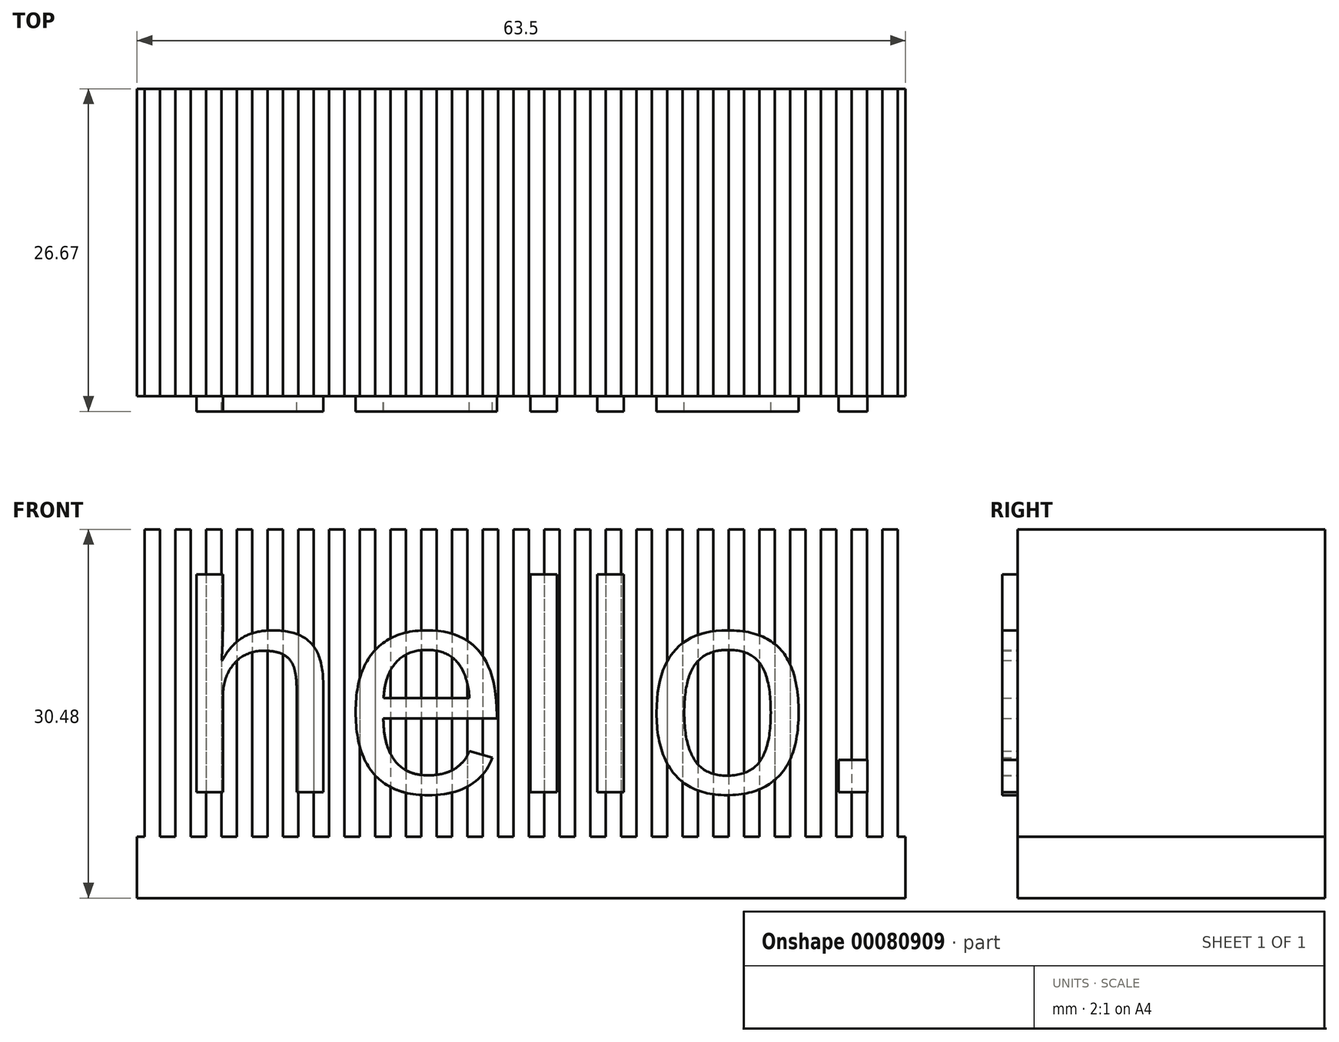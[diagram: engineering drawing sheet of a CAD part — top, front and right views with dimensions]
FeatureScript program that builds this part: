
annotation { "Feature Type Name" : "Feature", "Feature Type Description" : "" }
export const myFeature = defineFeature(function(context is Context, id is Id, definition is map)
    precondition{}
    {
        {
            var Q0;
            Q0=qCreatedBy(makeId("Top.planeOp"),FACE);
            var sketch = newSketch(context, id + "F0", { "sketchPlane" : qUnion([Q0])});
            skLineSegment(sketch, "E0.bottom", {"start": v(31.75, 12.7) * mm, "end": v(-31.75, 12.7) * mm});
            skLineSegment(sketch, "E0.top", {"start": v(31.75, -12.7) * mm, "end": v(-31.75, -12.7) * mm});
            skLineSegment(sketch, "E0.left", {"start": v(31.75, 12.7) * mm, "end": v(31.75, -12.7) * mm});
            skLineSegment(sketch, "E0.right", {"start": v(-31.75, 12.7) * mm, "end": v(-31.75, -12.7) * mm});
            skPoint(sketch, "E0.middle", {"position": v(0, 0) * mm});
            skSolve(sketch);
        }
        {
            var Q0;
            Q0=makeQuery(id+"F0.imprint","IMPRINT",FACE,{"disambiguationData":[TD([[makeQuery(id+"F0.imprint","IMPRINT",EDGE,{"derivedFrom":sQuery(id+"F0.wireOp",EDGE,"E0.bottom")}),1.0]])]});
            extrude(context, id + "F1", {"entities" : qUnion([Q0]), "depth" : 5.08 * mm});
        }
        {
            var Q0;
            Q0=makeQuery(id+"F1.opExtrude","CAP_FACE",FACE,{"disambiguationData":[OSD([sQuery(id+"F0.wireOp",EDGE,"E0.bottom"),sQuery(id+"F0.wireOp",EDGE,"E0.top"),sQuery(id+"F0.wireOp",EDGE,"E0.left"),sQuery(id+"F0.wireOp",EDGE,"E0.right")])],"isStart":false});
            var sketch = newSketch(context, id + "F2", { "sketchPlane" : qUnion([Q0])});
            skLineSegment(sketch, "E1.bottom", {"start": v(-29.84, -12.7) * mm, "end": v(-31.12, -12.7) * mm});
            skLineSegment(sketch, "E1.top", {"start": v(-29.84, 12.7) * mm, "end": v(-31.12, 12.7) * mm});
            skLineSegment(sketch, "E1.left", {"start": v(-29.84, -12.7) * mm, "end": v(-29.84, 12.7) * mm});
            skLineSegment(sketch, "E1.right", {"start": v(-31.12, -12.7) * mm, "end": v(-31.12, 12.7) * mm});
            skPoint(sketch, "E1.middle", {"position": v(-30.48, 0) * mm});
            skLineSegment(sketch, "E2.1.0.0", {"start": v(-28.57, -12.7) * mm, "end": v(-28.57, 12.7) * mm});
            skLineSegment(sketch, "E2.1.0.1", {"start": v(-27.3, -12.7) * mm, "end": v(-27.3, 12.7) * mm});
            skLineSegment(sketch, "E2.1.0.2", {"start": v(-27.3, 12.7) * mm, "end": v(-28.57, 12.7) * mm});
            skLineSegment(sketch, "E2.1.0.3", {"start": v(-27.3, -12.7) * mm, "end": v(-28.57, -12.7) * mm});
            skLineSegment(sketch, "E2.2.0.0", {"start": v(-26.04, -12.7) * mm, "end": v(-26.04, 12.7) * mm});
            skLineSegment(sketch, "E2.2.0.1", {"start": v(-24.77, -12.7) * mm, "end": v(-24.77, 12.7) * mm});
            skLineSegment(sketch, "E2.2.0.2", {"start": v(-24.77, 12.7) * mm, "end": v(-26.04, 12.7) * mm});
            skLineSegment(sketch, "E2.2.0.3", {"start": v(-24.77, -12.7) * mm, "end": v(-26.04, -12.7) * mm});
            skLineSegment(sketch, "E2.3.0.0", {"start": v(-23.5, -12.7) * mm, "end": v(-23.5, 12.7) * mm});
            skLineSegment(sketch, "E2.3.0.1", {"start": v(-22.22, -12.7) * mm, "end": v(-22.22, 12.7) * mm});
            skLineSegment(sketch, "E2.3.0.2", {"start": v(-22.22, 12.7) * mm, "end": v(-23.5, 12.7) * mm});
            skLineSegment(sketch, "E2.3.0.3", {"start": v(-22.22, -12.7) * mm, "end": v(-23.5, -12.7) * mm});
            skLineSegment(sketch, "E2.4.0.0", {"start": v(-20.95, -12.7) * mm, "end": v(-20.95, 12.7) * mm});
            skLineSegment(sketch, "E2.4.0.1", {"start": v(-19.68, -12.7) * mm, "end": v(-19.68, 12.7) * mm});
            skLineSegment(sketch, "E2.4.0.2", {"start": v(-19.68, 12.7) * mm, "end": v(-20.95, 12.7) * mm});
            skLineSegment(sketch, "E2.4.0.3", {"start": v(-19.68, -12.7) * mm, "end": v(-20.95, -12.7) * mm});
            skLineSegment(sketch, "E2.5.0.0", {"start": v(-18.41, -12.7) * mm, "end": v(-18.41, 12.7) * mm});
            skLineSegment(sketch, "E2.5.0.1", {"start": v(-17.14, -12.7) * mm, "end": v(-17.14, 12.7) * mm});
            skLineSegment(sketch, "E2.5.0.2", {"start": v(-17.14, 12.7) * mm, "end": v(-18.41, 12.7) * mm});
            skLineSegment(sketch, "E2.5.0.3", {"start": v(-17.14, -12.7) * mm, "end": v(-18.41, -12.7) * mm});
            skLineSegment(sketch, "E2.6.0.0", {"start": v(-15.87, -12.7) * mm, "end": v(-15.87, 12.7) * mm});
            skLineSegment(sketch, "E2.6.0.1", {"start": v(-14.6, -12.7) * mm, "end": v(-14.6, 12.7) * mm});
            skLineSegment(sketch, "E2.6.0.2", {"start": v(-14.6, 12.7) * mm, "end": v(-15.87, 12.7) * mm});
            skLineSegment(sketch, "E2.6.0.3", {"start": v(-14.6, -12.7) * mm, "end": v(-15.87, -12.7) * mm});
            skLineSegment(sketch, "E2.7.0.0", {"start": v(-13.33, -12.7) * mm, "end": v(-13.33, 12.7) * mm});
            skLineSegment(sketch, "E2.7.0.1", {"start": v(-12.06, -12.7) * mm, "end": v(-12.06, 12.7) * mm});
            skLineSegment(sketch, "E2.7.0.2", {"start": v(-12.06, 12.7) * mm, "end": v(-13.33, 12.7) * mm});
            skLineSegment(sketch, "E2.7.0.3", {"start": v(-12.06, -12.7) * mm, "end": v(-13.33, -12.7) * mm});
            skLineSegment(sketch, "E2.8.0.0", {"start": v(-10.8, -12.7) * mm, "end": v(-10.8, 12.7) * mm});
            skLineSegment(sketch, "E2.8.0.1", {"start": v(-9.52, -12.7) * mm, "end": v(-9.52, 12.7) * mm});
            skLineSegment(sketch, "E2.8.0.2", {"start": v(-9.52, 12.7) * mm, "end": v(-10.8, 12.7) * mm});
            skLineSegment(sketch, "E2.8.0.3", {"start": v(-9.52, -12.7) * mm, "end": v(-10.8, -12.7) * mm});
            skLineSegment(sketch, "E2.9.0.0", {"start": v(-8.25, -12.7) * mm, "end": v(-8.25, 12.7) * mm});
            skLineSegment(sketch, "E2.9.0.1", {"start": v(-6.98, -12.7) * mm, "end": v(-6.98, 12.7) * mm});
            skLineSegment(sketch, "E2.9.0.2", {"start": v(-6.98, 12.7) * mm, "end": v(-8.25, 12.7) * mm});
            skLineSegment(sketch, "E2.9.0.3", {"start": v(-6.98, -12.7) * mm, "end": v(-8.25, -12.7) * mm});
            skLineSegment(sketch, "E2.10.0.0", {"start": v(-5.71, -12.7) * mm, "end": v(-5.71, 12.7) * mm});
            skLineSegment(sketch, "E2.10.0.1", {"start": v(-4.44, -12.7) * mm, "end": v(-4.44, 12.7) * mm});
            skLineSegment(sketch, "E2.10.0.2", {"start": v(-4.44, 12.7) * mm, "end": v(-5.71, 12.7) * mm});
            skLineSegment(sketch, "E2.10.0.3", {"start": v(-4.44, -12.7) * mm, "end": v(-5.71, -12.7) * mm});
            skLineSegment(sketch, "E2.11.0.0", {"start": v(-3.17, -12.7) * mm, "end": v(-3.17, 12.7) * mm});
            skLineSegment(sketch, "E2.11.0.1", {"start": v(-1.9, -12.7) * mm, "end": v(-1.9, 12.7) * mm});
            skLineSegment(sketch, "E2.11.0.2", {"start": v(-1.9, 12.7) * mm, "end": v(-3.17, 12.7) * mm});
            skLineSegment(sketch, "E2.11.0.3", {"start": v(-1.9, -12.7) * mm, "end": v(-3.17, -12.7) * mm});
            skLineSegment(sketch, "E2.12.0.0", {"start": v(-0.63, -12.7) * mm, "end": v(-0.63, 12.7) * mm});
            skLineSegment(sketch, "E2.12.0.1", {"start": v(0.64, -12.7) * mm, "end": v(0.64, 12.7) * mm});
            skLineSegment(sketch, "E2.12.0.2", {"start": v(0.64, 12.7) * mm, "end": v(-0.63, 12.7) * mm});
            skLineSegment(sketch, "E2.12.0.3", {"start": v(0.64, -12.7) * mm, "end": v(-0.63, -12.7) * mm});
            skLineSegment(sketch, "E2.13.0.0", {"start": v(1.9, -12.7) * mm, "end": v(1.9, 12.7) * mm});
            skLineSegment(sketch, "E2.13.0.1", {"start": v(3.18, -12.7) * mm, "end": v(3.18, 12.7) * mm});
            skLineSegment(sketch, "E2.13.0.2", {"start": v(3.18, 12.7) * mm, "end": v(1.9, 12.7) * mm});
            skLineSegment(sketch, "E2.13.0.3", {"start": v(3.18, -12.7) * mm, "end": v(1.9, -12.7) * mm});
            skLineSegment(sketch, "E2.14.0.0", {"start": v(4.45, -12.7) * mm, "end": v(4.45, 12.7) * mm});
            skLineSegment(sketch, "E2.14.0.1", {"start": v(5.72, -12.7) * mm, "end": v(5.72, 12.7) * mm});
            skLineSegment(sketch, "E2.14.0.2", {"start": v(5.72, 12.7) * mm, "end": v(4.45, 12.7) * mm});
            skLineSegment(sketch, "E2.14.0.3", {"start": v(5.72, -12.7) * mm, "end": v(4.45, -12.7) * mm});
            skLineSegment(sketch, "E2.15.0.0", {"start": v(6.99, -12.7) * mm, "end": v(6.99, 12.7) * mm});
            skLineSegment(sketch, "E2.15.0.1", {"start": v(8.26, -12.7) * mm, "end": v(8.26, 12.7) * mm});
            skLineSegment(sketch, "E2.15.0.2", {"start": v(8.26, 12.7) * mm, "end": v(6.99, 12.7) * mm});
            skLineSegment(sketch, "E2.15.0.3", {"start": v(8.26, -12.7) * mm, "end": v(6.99, -12.7) * mm});
            skLineSegment(sketch, "E2.16.0.0", {"start": v(9.53, -12.7) * mm, "end": v(9.53, 12.7) * mm});
            skLineSegment(sketch, "E2.16.0.1", {"start": v(10.8, -12.7) * mm, "end": v(10.8, 12.7) * mm});
            skLineSegment(sketch, "E2.16.0.2", {"start": v(10.8, 12.7) * mm, "end": v(9.53, 12.7) * mm});
            skLineSegment(sketch, "E2.16.0.3", {"start": v(10.8, -12.7) * mm, "end": v(9.53, -12.7) * mm});
            skLineSegment(sketch, "E2.17.0.0", {"start": v(12.07, -12.7) * mm, "end": v(12.07, 12.7) * mm});
            skLineSegment(sketch, "E2.17.0.1", {"start": v(13.34, -12.7) * mm, "end": v(13.34, 12.7) * mm});
            skLineSegment(sketch, "E2.17.0.2", {"start": v(13.34, 12.7) * mm, "end": v(12.07, 12.7) * mm});
            skLineSegment(sketch, "E2.17.0.3", {"start": v(13.34, -12.7) * mm, "end": v(12.07, -12.7) * mm});
            skLineSegment(sketch, "E2.18.0.0", {"start": v(14.6, -12.7) * mm, "end": v(14.6, 12.7) * mm});
            skLineSegment(sketch, "E2.18.0.1", {"start": v(15.88, -12.7) * mm, "end": v(15.88, 12.7) * mm});
            skLineSegment(sketch, "E2.18.0.2", {"start": v(15.88, 12.7) * mm, "end": v(14.6, 12.7) * mm});
            skLineSegment(sketch, "E2.18.0.3", {"start": v(15.88, -12.7) * mm, "end": v(14.6, -12.7) * mm});
            skLineSegment(sketch, "E2.19.0.0", {"start": v(17.15, -12.7) * mm, "end": v(17.15, 12.7) * mm});
            skLineSegment(sketch, "E2.19.0.1", {"start": v(18.42, -12.7) * mm, "end": v(18.42, 12.7) * mm});
            skLineSegment(sketch, "E2.19.0.2", {"start": v(18.42, 12.7) * mm, "end": v(17.15, 12.7) * mm});
            skLineSegment(sketch, "E2.19.0.3", {"start": v(18.42, -12.7) * mm, "end": v(17.15, -12.7) * mm});
            skLineSegment(sketch, "E2.20.0.0", {"start": v(19.69, -12.7) * mm, "end": v(19.69, 12.7) * mm});
            skLineSegment(sketch, "E2.20.0.1", {"start": v(20.96, -12.7) * mm, "end": v(20.96, 12.7) * mm});
            skLineSegment(sketch, "E2.20.0.2", {"start": v(20.96, 12.7) * mm, "end": v(19.69, 12.7) * mm});
            skLineSegment(sketch, "E2.20.0.3", {"start": v(20.96, -12.7) * mm, "end": v(19.69, -12.7) * mm});
            skLineSegment(sketch, "E2.21.0.0", {"start": v(22.23, -12.7) * mm, "end": v(22.23, 12.7) * mm});
            skLineSegment(sketch, "E2.21.0.1", {"start": v(23.5, -12.7) * mm, "end": v(23.5, 12.7) * mm});
            skLineSegment(sketch, "E2.21.0.2", {"start": v(23.5, 12.7) * mm, "end": v(22.23, 12.7) * mm});
            skLineSegment(sketch, "E2.21.0.3", {"start": v(23.5, -12.7) * mm, "end": v(22.23, -12.7) * mm});
            skLineSegment(sketch, "E2.22.0.0", {"start": v(24.77, -12.7) * mm, "end": v(24.77, 12.7) * mm});
            skLineSegment(sketch, "E2.22.0.1", {"start": v(26.04, -12.7) * mm, "end": v(26.04, 12.7) * mm});
            skLineSegment(sketch, "E2.22.0.2", {"start": v(26.04, 12.7) * mm, "end": v(24.77, 12.7) * mm});
            skLineSegment(sketch, "E2.22.0.3", {"start": v(26.04, -12.7) * mm, "end": v(24.77, -12.7) * mm});
            skLineSegment(sketch, "E2.23.0.0", {"start": v(27.3, -12.7) * mm, "end": v(27.3, 12.7) * mm});
            skLineSegment(sketch, "E2.23.0.1", {"start": v(28.58, -12.7) * mm, "end": v(28.58, 12.7) * mm});
            skLineSegment(sketch, "E2.23.0.2", {"start": v(28.58, 12.7) * mm, "end": v(27.3, 12.7) * mm});
            skLineSegment(sketch, "E2.23.0.3", {"start": v(28.58, -12.7) * mm, "end": v(27.3, -12.7) * mm});
            skLineSegment(sketch, "E2.24.0.0", {"start": v(29.85, -12.7) * mm, "end": v(29.85, 12.7) * mm});
            skLineSegment(sketch, "E2.24.0.1", {"start": v(31.12, -12.7) * mm, "end": v(31.12, 12.7) * mm});
            skLineSegment(sketch, "E2.24.0.2", {"start": v(31.12, 12.7) * mm, "end": v(29.85, 12.7) * mm});
            skLineSegment(sketch, "E2.24.0.3", {"start": v(31.12, -12.7) * mm, "end": v(29.85, -12.7) * mm});
            skLineSegment(sketch, "E2.direction1", {"start": v(-31.12, -12.7) * mm, "end": v(-28.57, -12.7) * mm, "construction": true});
            skSolve(sketch);
        }
        {
            var Q0;
            Q0 = qSketchRegion(id + "F2", true);
            extrude(context, id + "F3", {"entities" : qUnion([Q0]), "operationType" : NewBodyOperationType.ADD, "depth" : 25.4 * mm});
        }
        {
            var Q0;
            Q0=makeQuery(id+"F3.boolean.opBoolean","MERGE",FACE,{"derivedFrom":[makeQuery(id+"F1.opExtrude","SWEPT_FACE",FACE,{"disambiguationData":[OSD([sQuery(id+"F0.wireOp",EDGE,"E0.top")])]}),makeQuery(id+"F3.opExtrude","SWEPT_FACE",FACE,{"disambiguationData":[OSD([sQuery(id+"F2.wireOp",EDGE,"E1.bottom")])]}),makeQuery(id+"F3.opExtrude","SWEPT_FACE",FACE,{"disambiguationData":[OSD([sQuery(id+"F2.wireOp",EDGE,"E2.1.0.3")])]}),makeQuery(id+"F3.opExtrude","SWEPT_FACE",FACE,{"disambiguationData":[OSD([sQuery(id+"F2.wireOp",EDGE,"E2.2.0.3")])]}),makeQuery(id+"F3.opExtrude","SWEPT_FACE",FACE,{"disambiguationData":[OSD([sQuery(id+"F2.wireOp",EDGE,"E2.3.0.3")])]}),makeQuery(id+"F3.opExtrude","SWEPT_FACE",FACE,{"disambiguationData":[OSD([sQuery(id+"F2.wireOp",EDGE,"E2.4.0.3")])]}),makeQuery(id+"F3.opExtrude","SWEPT_FACE",FACE,{"disambiguationData":[OSD([sQuery(id+"F2.wireOp",EDGE,"E2.5.0.3")])]}),makeQuery(id+"F3.opExtrude","SWEPT_FACE",FACE,{"disambiguationData":[OSD([sQuery(id+"F2.wireOp",EDGE,"E2.6.0.3")])]}),makeQuery(id+"F3.opExtrude","SWEPT_FACE",FACE,{"disambiguationData":[OSD([sQuery(id+"F2.wireOp",EDGE,"E2.7.0.3")])]}),makeQuery(id+"F3.opExtrude","SWEPT_FACE",FACE,{"disambiguationData":[OSD([sQuery(id+"F2.wireOp",EDGE,"E2.8.0.3")])]}),makeQuery(id+"F3.opExtrude","SWEPT_FACE",FACE,{"disambiguationData":[OSD([sQuery(id+"F2.wireOp",EDGE,"E2.9.0.3")])]}),makeQuery(id+"F3.opExtrude","SWEPT_FACE",FACE,{"disambiguationData":[OSD([sQuery(id+"F2.wireOp",EDGE,"E2.10.0.3")])]}),makeQuery(id+"F3.opExtrude","SWEPT_FACE",FACE,{"disambiguationData":[OSD([sQuery(id+"F2.wireOp",EDGE,"E2.11.0.3")])]}),makeQuery(id+"F3.opExtrude","SWEPT_FACE",FACE,{"disambiguationData":[OSD([sQuery(id+"F2.wireOp",EDGE,"E2.12.0.3")])]}),makeQuery(id+"F3.opExtrude","SWEPT_FACE",FACE,{"disambiguationData":[OSD([sQuery(id+"F2.wireOp",EDGE,"E2.13.0.3")])]}),makeQuery(id+"F3.opExtrude","SWEPT_FACE",FACE,{"disambiguationData":[OSD([sQuery(id+"F2.wireOp",EDGE,"E2.14.0.3")])]}),makeQuery(id+"F3.opExtrude","SWEPT_FACE",FACE,{"disambiguationData":[OSD([sQuery(id+"F2.wireOp",EDGE,"E2.15.0.3")])]}),makeQuery(id+"F3.opExtrude","SWEPT_FACE",FACE,{"disambiguationData":[OSD([sQuery(id+"F2.wireOp",EDGE,"E2.16.0.3")])]}),makeQuery(id+"F3.opExtrude","SWEPT_FACE",FACE,{"disambiguationData":[OSD([sQuery(id+"F2.wireOp",EDGE,"E2.17.0.3")])]}),makeQuery(id+"F3.opExtrude","SWEPT_FACE",FACE,{"disambiguationData":[OSD([sQuery(id+"F2.wireOp",EDGE,"E2.18.0.3")])]}),makeQuery(id+"F3.opExtrude","SWEPT_FACE",FACE,{"disambiguationData":[OSD([sQuery(id+"F2.wireOp",EDGE,"E2.19.0.3")])]}),makeQuery(id+"F3.opExtrude","SWEPT_FACE",FACE,{"disambiguationData":[OSD([sQuery(id+"F2.wireOp",EDGE,"E2.20.0.3")])]}),makeQuery(id+"F3.opExtrude","SWEPT_FACE",FACE,{"disambiguationData":[OSD([sQuery(id+"F2.wireOp",EDGE,"E2.21.0.3")])]}),makeQuery(id+"F3.opExtrude","SWEPT_FACE",FACE,{"disambiguationData":[OSD([sQuery(id+"F2.wireOp",EDGE,"E2.22.0.3")])]}),makeQuery(id+"F3.opExtrude","SWEPT_FACE",FACE,{"disambiguationData":[OSD([sQuery(id+"F2.wireOp",EDGE,"E2.23.0.3")])]}),makeQuery(id+"F3.opExtrude","SWEPT_FACE",FACE,{"disambiguationData":[OSD([sQuery(id+"F2.wireOp",EDGE,"E2.24.0.3")])]})]});
            var sketch = newSketch(context, id + "F4", { "sketchPlane" : qUnion([Q0])});
            skText(sketch, "E3", { "text": "hello.", "fontName": "Arimo-Regular.ttf"});
            const initialGuessF4  = {"E3": [-0.02857, 0.00875, 1, 0, 0.0179]};
            skSetInitialGuess(sketch, initialGuessF4);
            skSolve(sketch);
        }
        {
            var Q0;
            Q0 = qSketchRegion(id + "F4", true);
            extrude(context, id + "F5", {"entities" : qUnion([Q0]), "operationType" : NewBodyOperationType.ADD, "depth" : 1.27 * mm});
        }
    });
